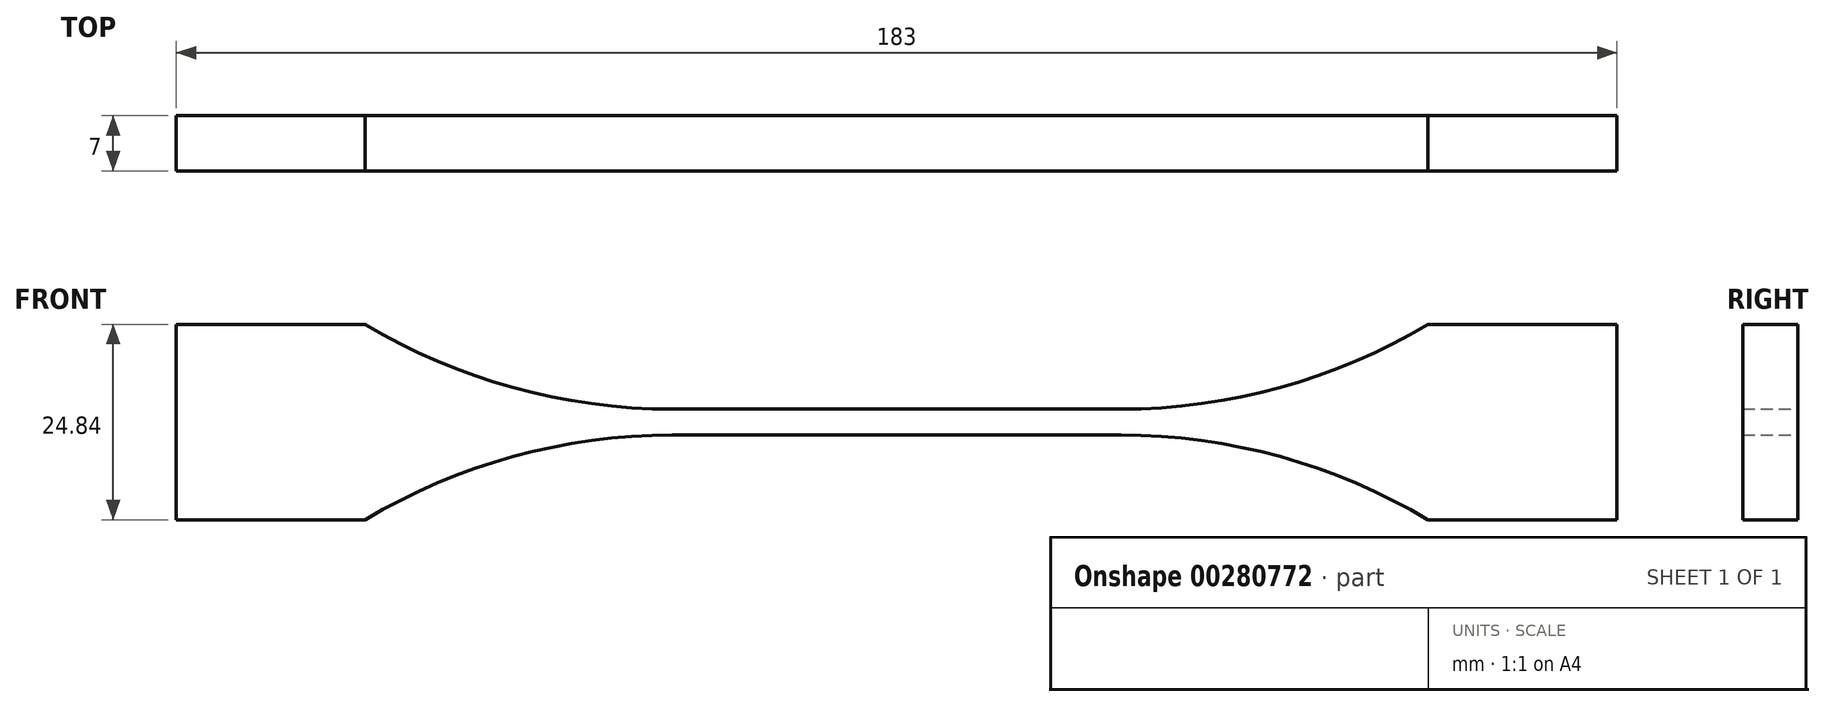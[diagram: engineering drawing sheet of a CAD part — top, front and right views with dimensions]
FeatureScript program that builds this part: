
annotation { "Feature Type Name" : "Feature", "Feature Type Description" : "" }
export const myFeature = defineFeature(function(context is Context, id is Id, definition is map)
    precondition{}
    {
        {
            var Q0;
            Q0=qCreatedBy(makeId("Front.planeOp"),FACE);
            var sketch = newSketch(context, id + "F0", { "sketchPlane" : qUnion([Q0])});
            skLineSegment(sketch, "E0", {"start": v(0, 1.65) * mm, "end": v(28.5, 1.65) * mm});
            skArc(sketch, "E1", {"start": v(28.5, 1.65) * mm, "mid": v(48.73, 4.39) * mm, "end": v(67.5, 12.42) * mm});
            skLineSegment(sketch, "E2", {"start": v(67.5, 12.42) * mm, "end": v(91.5, 12.42) * mm});
            skLineSegment(sketch, "E3.MirrorCS", {"start": v(0, -1.65) * mm, "end": v(28.5, -1.65) * mm});
            skLineSegment(sketch, "E4.MirrorCS", {"start": v(67.5, -12.42) * mm, "end": v(91.5, -12.42) * mm});
            skArc(sketch, "E5.MirrorCS", {"start": v(28.5, -1.65) * mm, "mid": v(48.73, -4.39) * mm, "end": v(67.5, -12.42) * mm});
            skLineSegment(sketch, "E6.MirrorCS", {"start": v(0, 1.65) * mm, "end": v(-28.5, 1.65) * mm});
            skArc(sketch, "E7.MirrorCS", {"start": v(-28.5, 1.65) * mm, "mid": v(-48.73, 4.39) * mm, "end": v(-67.5, 12.42) * mm});
            skLineSegment(sketch, "E8.MirrorCS", {"start": v(-67.5, 12.42) * mm, "end": v(-91.5, 12.42) * mm});
            skLineSegment(sketch, "E9.MirrorCS", {"start": v(0, -1.65) * mm, "end": v(-28.5, -1.65) * mm});
            skArc(sketch, "E10.MirrorCS", {"start": v(-28.5, -1.65) * mm, "mid": v(-48.73, -4.39) * mm, "end": v(-67.5, -12.42) * mm});
            skLineSegment(sketch, "E11.MirrorCS", {"start": v(-67.5, -12.42) * mm, "end": v(-91.5, -12.42) * mm});
            skLineSegment(sketch, "E12", {"start": v(91.5, 12.42) * mm, "end": v(91.5, -12.42) * mm});
            skLineSegment(sketch, "E13", {"start": v(-91.5, 12.42) * mm, "end": v(-91.5, -12.42) * mm});
            skSolve(sketch);
        }
        {
            var Q0;
            Q0 = qSketchRegion(id + "F0", true);
            extrude(context, id + "F1", {"entities" : qUnion([Q0]), "endBound" : BoundingType.SYMMETRIC, "depth" : 7 * mm});
        }
    });
